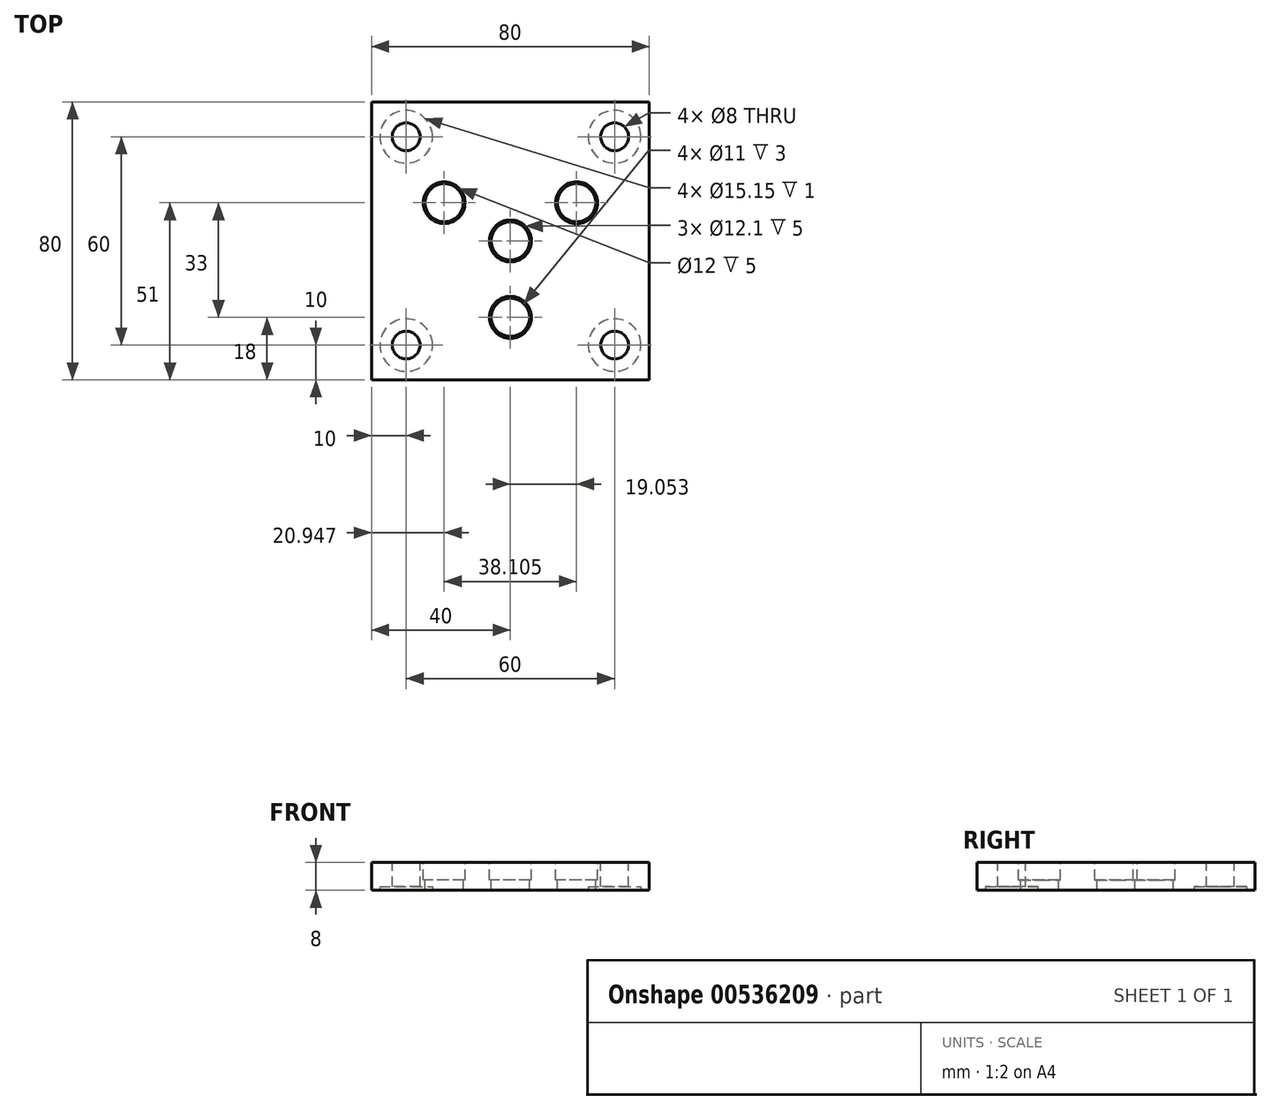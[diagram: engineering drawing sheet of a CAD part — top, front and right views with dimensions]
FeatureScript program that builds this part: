
annotation { "Feature Type Name" : "Feature", "Feature Type Description" : "" }
export const myFeature = defineFeature(function(context is Context, id is Id, definition is map)
    precondition{}
    {
        {
            var Q0;
            Q0=qCreatedBy(makeId("Top.planeOp"),FACE);
            var sketch = newSketch(context, id + "F0", { "sketchPlane" : qUnion([Q0])});
            skLineSegment(sketch, "E0.bottom", {"start": v(40, -40) * mm, "end": v(-40, -40) * mm});
            skLineSegment(sketch, "E0.top", {"start": v(40, 40) * mm, "end": v(-40, 40) * mm});
            skLineSegment(sketch, "E0.left", {"start": v(40, -40) * mm, "end": v(40, 40) * mm});
            skLineSegment(sketch, "E0.right", {"start": v(-40, -40) * mm, "end": v(-40, 40) * mm});
            skPoint(sketch, "E0.middle", {"position": v(0, 0) * mm});
            skSolve(sketch);
        }
        {
            var Q0;
            Q0=makeQuery(id+"F0.imprint","IMPRINT",FACE,{"disambiguationData":[TD([[makeQuery(id+"F0.imprint","IMPRINT",EDGE,{"derivedFrom":sQuery(id+"F0.wireOp",EDGE,"E0.bottom")}),-1.0]])]});
            extrude(context, id + "F1", {"entities" : qUnion([Q0]), "depth" : 8 * mm, "offsetDistance" : 25 * mm});
        }
        {
            var Q0;
            Q0=makeQuery(id+"F1.opExtrude","CAP_FACE",FACE,{"disambiguationData":[OSD([sQuery(id+"F0.wireOp",EDGE,"E0.bottom"),sQuery(id+"F0.wireOp",EDGE,"E0.top"),sQuery(id+"F0.wireOp",EDGE,"E0.left"),sQuery(id+"F0.wireOp",EDGE,"E0.right")])],"isStart":false});
            var sketch = newSketch(context, id + "F2", { "sketchPlane" : qUnion([Q0])});
            skCircle(sketch, "E1", {"center": v(0, 0) * mm, "radius": 5.5 * mm});
            skLineSegment(sketch, "E2", {"start": v(0, 0) * mm, "end": v(0, -22) * mm, "construction": true});
            skCircle(sketch, "E3", {"center": v(0, -22) * mm, "radius": 5.5 * mm});
            skCircle(sketch, "E4.1.0", {"center": v(19.05, 11) * mm, "radius": 5.5 * mm});
            skCircle(sketch, "E4.2.0", {"center": v(-19.05, 11) * mm, "radius": 5.5 * mm});
            skLineSegment(sketch, "E5.bottom", {"start": v(-40, 40) * mm, "end": v(-30, 40) * mm, "construction": true});
            skLineSegment(sketch, "E5.top", {"start": v(-40, 30) * mm, "end": v(-30, 30) * mm, "construction": true});
            skLineSegment(sketch, "E5.left", {"start": v(-40, 40) * mm, "end": v(-40, 30) * mm, "construction": true});
            skLineSegment(sketch, "E5.right", {"start": v(-30, 40) * mm, "end": v(-30, 30) * mm, "construction": true});
            skCircle(sketch, "E6", {"center": v(-30, 30) * mm, "radius": 4 * mm});
            skCircle(sketch, "E7.0.1.0", {"center": v(-30, -30) * mm, "radius": 4 * mm});
            skCircle(sketch, "E7.1.0.0", {"center": v(30, 30) * mm, "radius": 4 * mm});
            skCircle(sketch, "E7.1.1.0", {"center": v(30, -30) * mm, "radius": 4 * mm});
            skLineSegment(sketch, "E7.direction1", {"start": v(-30, 30) * mm, "end": v(30, 30) * mm, "construction": true});
            skLineSegment(sketch, "E7.direction2", {"start": v(-30, 30) * mm, "end": v(-30, -30) * mm, "construction": true});
            skSolve(sketch);
        }
        {
            var Q0;
            Q0=makeQuery(id+"F2.imprint","IMPRINT",FACE,{"disambiguationData":[TD([[makeQuery(id+"F2.imprint","IMPRINT",EDGE,{"derivedFrom":sQuery(id+"F2.wireOp",EDGE,"E4.2.0")}),1.0]])]});
            var Q1;
            Q1=makeQuery(id+"F2.imprint","IMPRINT",FACE,{"disambiguationData":[TD([[makeQuery(id+"F2.imprint","IMPRINT",EDGE,{"derivedFrom":sQuery(id+"F2.wireOp",EDGE,"E6")}),1.0]])]});
            var Q2;
            Q2=makeQuery(id+"F2.imprint","IMPRINT",FACE,{"disambiguationData":[TD([[makeQuery(id+"F2.imprint","IMPRINT",EDGE,{"derivedFrom":sQuery(id+"F2.wireOp",EDGE,"E4.1.0")}),1.0]])]});
            var Q3;
            Q3=makeQuery(id+"F2.imprint","IMPRINT",FACE,{"disambiguationData":[TD([[makeQuery(id+"F2.imprint","IMPRINT",EDGE,{"derivedFrom":sQuery(id+"F2.wireOp",EDGE,"E7.1.0.0")}),1.0]])]});
            var Q4;
            Q4=makeQuery(id+"F2.imprint","IMPRINT",FACE,{"disambiguationData":[TD([[makeQuery(id+"F2.imprint","IMPRINT",EDGE,{"derivedFrom":sQuery(id+"F2.wireOp",EDGE,"E7.1.1.0")}),1.0]])]});
            var Q5;
            Q5=makeQuery(id+"F2.imprint","IMPRINT",FACE,{"disambiguationData":[TD([[makeQuery(id+"F2.imprint","IMPRINT",EDGE,{"derivedFrom":sQuery(id+"F2.wireOp",EDGE,"E3")}),1.0]])]});
            var Q6;
            Q6=makeQuery(id+"F2.imprint","IMPRINT",FACE,{"disambiguationData":[TD([[makeQuery(id+"F2.imprint","IMPRINT",EDGE,{"derivedFrom":sQuery(id+"F2.wireOp",EDGE,"E7.0.1.0")}),1.0]])]});
            var Q7;
            Q7=makeQuery(id+"F2.imprint","IMPRINT",FACE,{"disambiguationData":[TD([[makeQuery(id+"F2.imprint","IMPRINT",EDGE,{"derivedFrom":sQuery(id+"F2.wireOp",EDGE,"E1")}),1.0]])]});
            extrude(context, id + "F3", {"entities" : qUnion([Q0, Q1, Q2, Q3, Q4, Q5, Q6, Q7]), "operationType" : NewBodyOperationType.REMOVE, "oppositeDirection" : true, "depth" : 25 * mm, "offsetDistance" : 25 * mm});
        }
        {
            var Q0;
            Q0=makeQuery(id+"F1.opExtrude","CAP_FACE",FACE,{"disambiguationData":[OSD([sQuery(id+"F0.wireOp",EDGE,"E0.bottom"),sQuery(id+"F0.wireOp",EDGE,"E0.top"),sQuery(id+"F0.wireOp",EDGE,"E0.left"),sQuery(id+"F0.wireOp",EDGE,"E0.right")])],"isStart":false});
            var sketch = newSketch(context, id + "F4", { "sketchPlane" : qUnion([Q0])});
            skCircle(sketch, "E8", {"center": v(0, 0) * mm, "radius": 6.05 * mm});
            skCircle(sketch, "E9", {"center": v(-19.05, 11) * mm, "radius": 6 * mm});
            skCircle(sketch, "E10", {"center": v(19.05, 11) * mm, "radius": 6.05 * mm});
            skCircle(sketch, "E11", {"center": v(0, -22) * mm, "radius": 6.05 * mm});
            skSolve(sketch);
        }
        {
            var Q0;
            Q0=makeQuery(id+"F4.imprint","IMPRINT",FACE,{"disambiguationData":[TD([[makeQuery(id+"F4.imprint","IMPRINT",EDGE,{"derivedFrom":sQuery(id+"F4.wireOp",EDGE,"E9")}),1.0]])]});
            var Q1;
            Q1=makeQuery(id+"F4.imprint","IMPRINT",FACE,{"disambiguationData":[TD([[makeQuery(id+"F4.imprint","IMPRINT",EDGE,{"derivedFrom":sQuery(id+"F4.wireOp",EDGE,"E10")}),1.0]])]});
            var Q2;
            Q2=makeQuery(id+"F4.imprint","IMPRINT",FACE,{"disambiguationData":[TD([[makeQuery(id+"F4.imprint","IMPRINT",EDGE,{"derivedFrom":sQuery(id+"F4.wireOp",EDGE,"E8")}),1.0]])]});
            var Q3;
            Q3=makeQuery(id+"F4.imprint","IMPRINT",FACE,{"disambiguationData":[TD([[makeQuery(id+"F4.imprint","IMPRINT",EDGE,{"derivedFrom":sQuery(id+"F4.wireOp",EDGE,"E11")}),1.0]])]});
            var Q4;
            Q4=sQuery(id+"F4.wireOp",EDGE,"E9");
            extrude(context, id + "F5", {"entities" : qUnion([Q0, Q1, Q2, Q3]), "operationType" : NewBodyOperationType.REMOVE, "surfaceEntities" : qUnion([Q4]), "oppositeDirection" : true, "depth" : 5 * mm, "offsetDistance" : 25 * mm});
        }
        {
            var Q0;
            Q0=makeQuery(id+"F1.opExtrude","CAP_FACE",FACE,{"disambiguationData":[OSD([sQuery(id+"F0.wireOp",EDGE,"E0.bottom"),sQuery(id+"F0.wireOp",EDGE,"E0.top"),sQuery(id+"F0.wireOp",EDGE,"E0.left"),sQuery(id+"F0.wireOp",EDGE,"E0.right")])],"isStart":true});
            var sketch = newSketch(context, id + "F6", { "sketchPlane" : qUnion([Q0])});
            skCircle(sketch, "E12", {"center": v(-30, 30) * mm, "radius": 7.58 * mm});
            skCircle(sketch, "E13", {"center": v(30, 30) * mm, "radius": 7.58 * mm});
            skCircle(sketch, "E14", {"center": v(-30, -30) * mm, "radius": 7.58 * mm});
            skCircle(sketch, "E15", {"center": v(30, -30) * mm, "radius": 7.58 * mm});
            skSolve(sketch);
        }
        {
            var Q0;
            Q0=makeQuery(id+"F6.imprint","IMPRINT",FACE,{"disambiguationData":[TD([[makeQuery(id+"F6.imprint","IMPRINT",EDGE,{"derivedFrom":sQuery(id+"F6.wireOp",EDGE,"E12")}),1.0]])]});
            var Q1;
            Q1=makeQuery(id+"F6.imprint","IMPRINT",FACE,{"disambiguationData":[TD([[makeQuery(id+"F6.imprint","IMPRINT",EDGE,{"derivedFrom":sQuery(id+"F6.wireOp",EDGE,"E13")}),1.0]])]});
            var Q2;
            Q2=makeQuery(id+"F6.imprint","IMPRINT",FACE,{"disambiguationData":[TD([[makeQuery(id+"F6.imprint","IMPRINT",EDGE,{"derivedFrom":sQuery(id+"F6.wireOp",EDGE,"E15")}),1.0]])]});
            var Q3;
            Q3=makeQuery(id+"F6.imprint","IMPRINT",FACE,{"disambiguationData":[TD([[makeQuery(id+"F6.imprint","IMPRINT",EDGE,{"derivedFrom":sQuery(id+"F6.wireOp",EDGE,"E14")}),1.0]])]});
            extrude(context, id + "F7", {"entities" : qUnion([Q0, Q1, Q2, Q3]), "operationType" : NewBodyOperationType.REMOVE, "oppositeDirection" : true, "depth" : 1 * mm, "offsetDistance" : 25 * mm});
        }
    });
